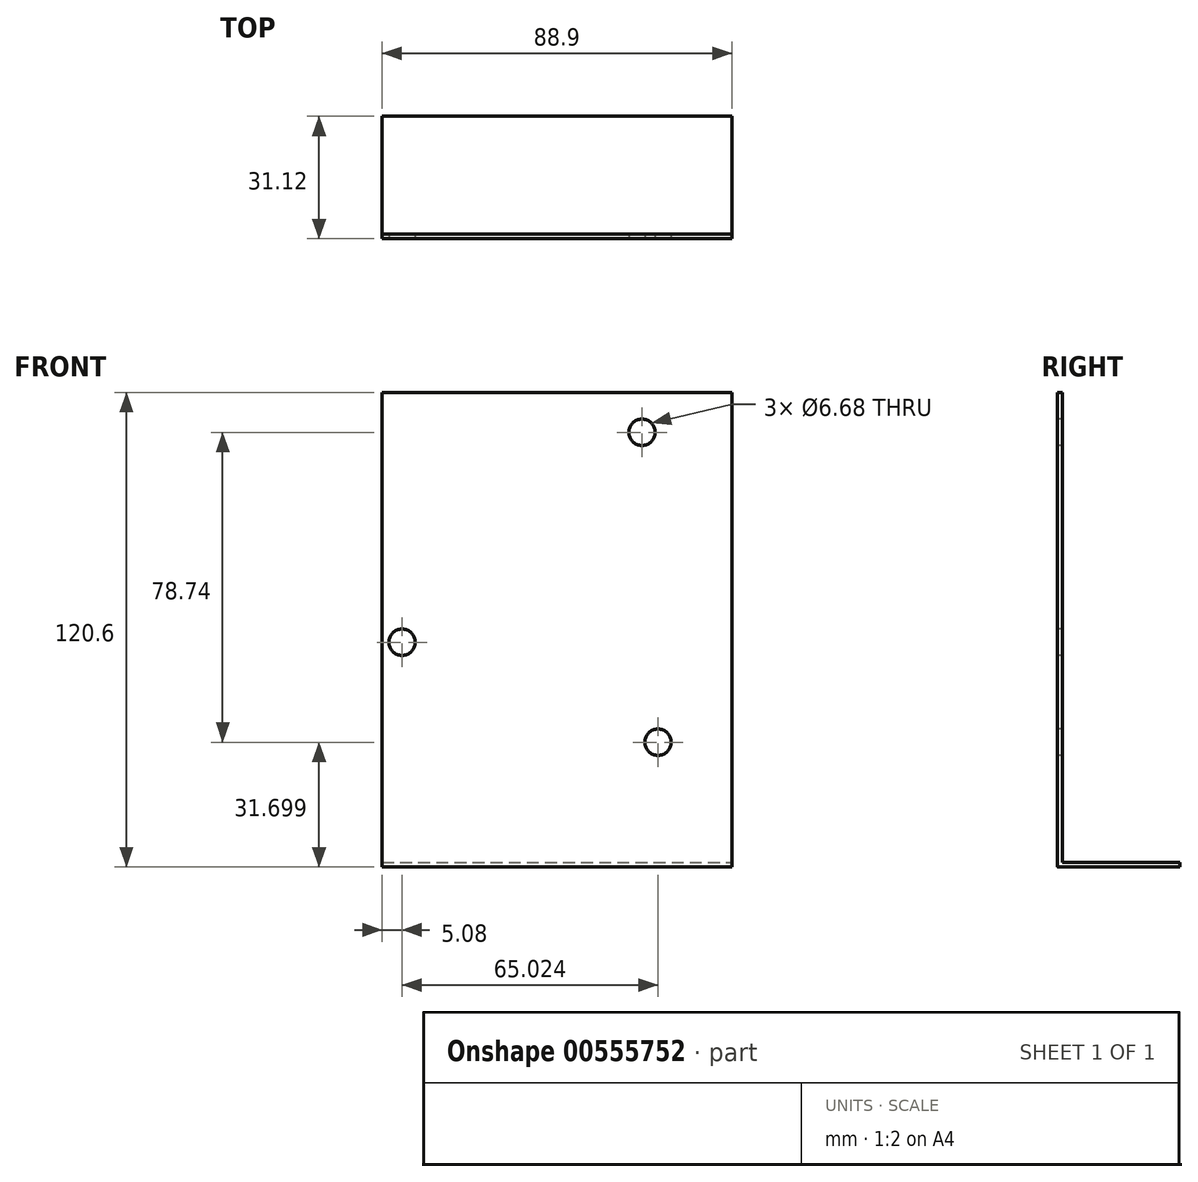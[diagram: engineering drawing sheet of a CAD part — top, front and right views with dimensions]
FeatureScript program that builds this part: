
annotation { "Feature Type Name" : "Feature", "Feature Type Description" : "" }
export const myFeature = defineFeature(function(context is Context, id is Id, definition is map)
    precondition{}
    {
        {
            var Q0;
            Q0=qCreatedBy(makeId("Top.planeOp"),FACE);
            var sketch = newSketch(context, id + "F0", { "sketchPlane" : qUnion([Q0])});
            skLineSegment(sketch, "E0.bottom", {"start": v(-44.45, -15.56) * mm, "end": v(44.45, -15.56) * mm});
            skLineSegment(sketch, "E0.top", {"start": v(-44.45, 15.56) * mm, "end": v(44.45, 15.56) * mm});
            skLineSegment(sketch, "E0.left", {"start": v(-44.45, -15.56) * mm, "end": v(-44.45, 15.56) * mm});
            skLineSegment(sketch, "E0.right", {"start": v(44.45, -15.56) * mm, "end": v(44.45, 15.56) * mm});
            skPoint(sketch, "E0.middle", {"position": v(0, 0) * mm});
            skSolve(sketch);
        }
        {
            var Q0;
            Q0 = qSketchRegion(id + "F0", true);
            extrude(context, id + "F1", {"entities" : qUnion([Q0]), "depth" : 1.22 * mm, "offsetDistance" : 25.4 * mm});
        }
        {
            var Q0;
            Q0=makeQuery(id+"F1.opExtrude","CAP_FACE",FACE,{"disambiguationData":[OSD([sQuery(id+"F0.wireOp",EDGE,"E0.bottom"),sQuery(id+"F0.wireOp",EDGE,"E0.top"),sQuery(id+"F0.wireOp",EDGE,"E0.left"),sQuery(id+"F0.wireOp",EDGE,"E0.right")])],"isStart":false});
            var sketch = newSketch(context, id + "F2", { "sketchPlane" : qUnion([Q0])});
            skLineSegment(sketch, "E1.bottom", {"start": v(44.45, -15.56) * mm, "end": v(-44.45, -15.56) * mm});
            skLineSegment(sketch, "E1.top", {"start": v(44.45, -14.34) * mm, "end": v(-44.45, -14.34) * mm});
            skLineSegment(sketch, "E1.left", {"start": v(44.45, -15.56) * mm, "end": v(44.45, -14.34) * mm});
            skLineSegment(sketch, "E1.right", {"start": v(-44.45, -15.56) * mm, "end": v(-44.45, -14.34) * mm});
            skSolve(sketch);
        }
        {
            var Q0;
            Q0 = qSketchRegion(id + "F2", true);
            extrude(context, id + "F3", {"entities" : qUnion([Q0]), "operationType" : NewBodyOperationType.ADD, "depth" : 119.38 * mm, "offsetDistance" : 25.4 * mm});
        }
        {
            var Q0;
            Q0=makeQuery(id+"F1.opExtrude","CAP_EDGE",EDGE,{"disambiguationData":[OSD([sQuery(id+"F0.wireOp",EDGE,"E0.bottom")])],"isStart":true});
            var Q1;
            Q1=makeQuery(id+"F3.opExtrude","CAP_EDGE",EDGE,{"disambiguationData":[OSD([sQuery(id+"F2.wireOp",EDGE,"E1.top")])],"isStart":true});
            fillet(context, id + "F4", {"entities" : qUnion([Q0, Q1]), "radius" : 0.05 * mm, "tangentPropagation" : true, "allowEdgeOverflow" : false});
        }
        {
            var Q0;
            Q0=makeQuery(id+"F3.boolean.opBoolean","MERGE",FACE,{"derivedFrom":[makeQuery(id+"F1.opExtrude","SWEPT_FACE",FACE,{"disambiguationData":[OSD([sQuery(id+"F0.wireOp",EDGE,"E0.bottom")])]}),makeQuery(id+"F3.opExtrude","SWEPT_FACE",FACE,{"disambiguationData":[OSD([sQuery(id+"F2.wireOp",EDGE,"E1.bottom")])]})]});
            var sketch = newSketch(context, id + "F5", { "sketchPlane" : qUnion([Q0])});
            skCircle(sketch, "E2", {"center": v(21.6, 110.44) * mm, "radius": 3.34 * mm});
            skCircle(sketch, "E3", {"center": v(-39.37, 57.1) * mm, "radius": 3.34 * mm});
            skCircle(sketch, "E4", {"center": v(25.65, 31.7) * mm, "radius": 3.34 * mm});
            skSolve(sketch);
        }
        {
            var Q0;
            Q0=makeQuery(id+"F5.imprint","IMPRINT",FACE,{"disambiguationData":[TD([[makeQuery(id+"F5.imprint","IMPRINT",EDGE,{"derivedFrom":sQuery(id+"F5.wireOp",EDGE,"E2")}),1.0]])]});
            var Q1;
            Q1=makeQuery(id+"F5.imprint","IMPRINT",FACE,{"disambiguationData":[TD([[makeQuery(id+"F5.imprint","IMPRINT",EDGE,{"derivedFrom":sQuery(id+"F5.wireOp",EDGE,"E4")}),1.0]])]});
            var Q2;
            Q2=makeQuery(id+"F5.imprint","IMPRINT",FACE,{"disambiguationData":[TD([[makeQuery(id+"F5.imprint","IMPRINT",EDGE,{"derivedFrom":sQuery(id+"F5.wireOp",EDGE,"E3")}),1.0]])]});
            extrude(context, id + "F6", {"entities" : qUnion([Q0, Q1, Q2]), "operationType" : NewBodyOperationType.REMOVE, "oppositeDirection" : true, "depth" : 25.4 * mm, "offsetDistance" : 25.4 * mm});
        }
    });
